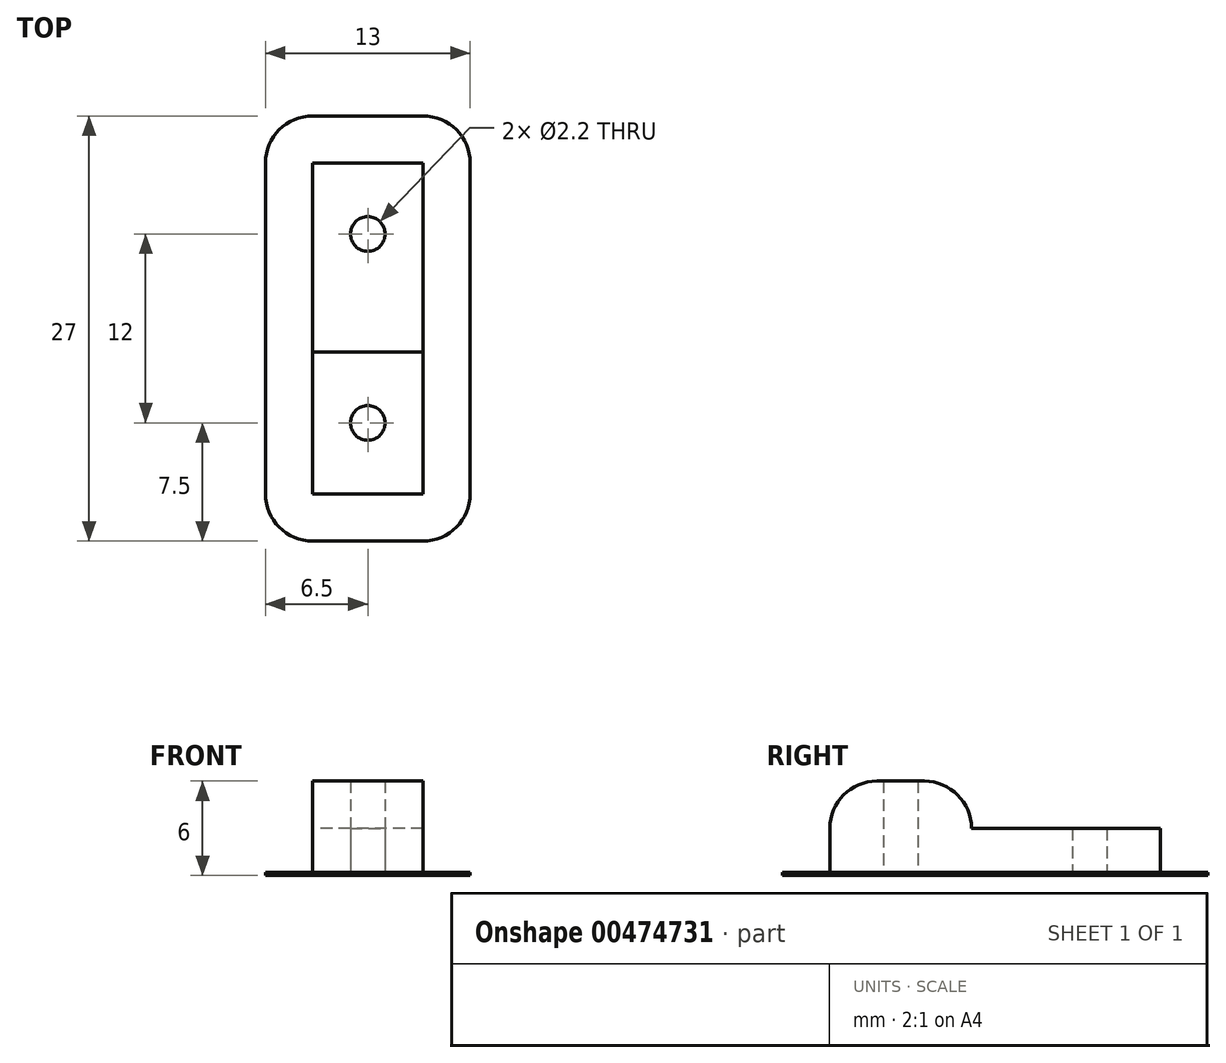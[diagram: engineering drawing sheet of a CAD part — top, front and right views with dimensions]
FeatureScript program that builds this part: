
annotation { "Feature Type Name" : "Feature", "Feature Type Description" : "" }
export const myFeature = defineFeature(function(context is Context, id is Id, definition is map)
    precondition{}
    {
        {
            var Q0;
            Q0=qCreatedBy(makeId("Right.planeOp"),FACE);
            var sketch = newSketch(context, id + "F0", { "sketchPlane" : qUnion([Q0])});
            skLineSegment(sketch, "E0", {"start": v(0, 0) * mm, "end": v(0, 3) * mm});
            skLineSegment(sketch, "E1", {"start": v(0, 0) * mm, "end": v(-21, 0) * mm});
            skLineSegment(sketch, "E2", {"start": v(-21, 0) * mm, "end": v(-21, 6) * mm});
            skLineSegment(sketch, "E3", {"start": v(0, 3) * mm, "end": v(-12, 3) * mm});
            skLineSegment(sketch, "E4", {"start": v(-12, 3) * mm, "end": v(-12, 6) * mm});
            skLineSegment(sketch, "E5", {"start": v(-12, 6) * mm, "end": v(-21, 6) * mm});
            skSolve(sketch);
        }
        {
            var Q0;
            Q0=qSketchRegion(id+"F0",true);
            extrude(context, id + "F1", {"entities" : qUnion([Q0]), "depth" : 7 * mm, "offsetDistance" : 25 * mm});
        }
        {
            var Q0;
            Q0=makeQuery(id+"F1.opExtrude","SWEPT_EDGE",EDGE,{"disambiguationData":[OSD([sQuery(id+"F0.wireOp",EDGE,"E4"),sQuery(id+"F0.wireOp",EDGE,"E5")])]});
            var Q1;
            Q1=makeQuery(id+"F1.opExtrude","SWEPT_EDGE",EDGE,{"disambiguationData":[OSD([sQuery(id+"F0.wireOp",EDGE,"E2"),sQuery(id+"F0.wireOp",EDGE,"E5")])]});
            fillet(context, id + "F2", {"entities" : qUnion([Q0, Q1]), "radius" : 3 * mm, "tangentPropagation" : true, "allowEdgeOverflow" : false});
        }
        {
            var Q0;
            Q0=makeQuery(id+"F1.opExtrude","SWEPT_FACE",FACE,{"disambiguationData":[OSD([sQuery(id+"F0.wireOp",EDGE,"E1")])]});
            var sketch = newSketch(context, id + "F3", { "sketchPlane" : qUnion([Q0])});
            skLineSegment(sketch, "E6", {"start": v(3.5, 21) * mm, "end": v(3.5, 0) * mm, "construction": true});
            skCircle(sketch, "E7", {"center": v(3.5, 16.5) * mm, "radius": 1.1 * mm});
            skCircle(sketch, "E8", {"center": v(3.5, 4.5) * mm, "radius": 1.1 * mm});
            skLineSegment(sketch, "E9", {"start": v(0, 10.5) * mm, "end": v(7, 10.5) * mm, "construction": true});
            skSolve(sketch);
        }
        {
            var Q0;
            Q0=qSketchRegion(id+"F3",true);
            extrude(context, id + "F4", {"entities" : qUnion([Q0]), "operationType" : NewBodyOperationType.REMOVE, "endBound" : BoundingType.THROUGH_ALL, "oppositeDirection" : true, "depth" : 25 * mm, "offsetDistance" : 25 * mm});
        }
        {
            var Q0;
            Q0=makeQuery(id+"F1.opExtrude","SWEPT_FACE",FACE,{"disambiguationData":[OSD([sQuery(id+"F0.wireOp",EDGE,"E1")])]});
            var sketch = newSketch(context, id + "F5", { "sketchPlane" : qUnion([Q0])});
            skLineSegment(sketch, "E10", {"start": v(0, 21) * mm, "end": v(7, 21) * mm});
            skLineSegment(sketch, "E11", {"start": v(7, 21) * mm, "end": v(7, 0) * mm});
            skLineSegment(sketch, "E12", {"start": v(7, 0) * mm, "end": v(0, 0) * mm});
            skLineSegment(sketch, "E13", {"start": v(0, 0) * mm, "end": v(0, 21) * mm});
            skLineSegment(sketch, "E14", {"start": v(-3, 21) * mm, "end": v(-3, 0) * mm});
            skLineSegment(sketch, "E15", {"start": v(0, 24) * mm, "end": v(7, 24) * mm});
            skLineSegment(sketch, "E16", {"start": v(10, 21) * mm, "end": v(10, 0) * mm});
            skLineSegment(sketch, "E17", {"start": v(0, -3) * mm, "end": v(7, -3) * mm});
            skArc(sketch, "E18", {"start": v(0, 24) * mm, "mid": v(-2.12, 23.12) * mm, "end": v(-3, 21) * mm});
            skArc(sketch, "E19", {"start": v(10, 21) * mm, "mid": v(9.12, 23.12) * mm, "end": v(7, 24) * mm});
            skArc(sketch, "E20", {"start": v(-3, 0) * mm, "mid": v(-2.12, -2.12) * mm, "end": v(0, -3) * mm});
            skArc(sketch, "E21", {"start": v(7, -3) * mm, "mid": v(9.12, -2.12) * mm, "end": v(10, 0) * mm});
            skSolve(sketch);
        }
        {
            var Q0;
            Q0 = qSketchRegion(id + "F5", true);
            extrude(context, id + "F6", {"entities" : qUnion([Q0]), "operationType" : NewBodyOperationType.ADD, "oppositeDirection" : true, "depth" : 0.2 * mm, "offsetDistance" : 25 * mm});
        }
    });
